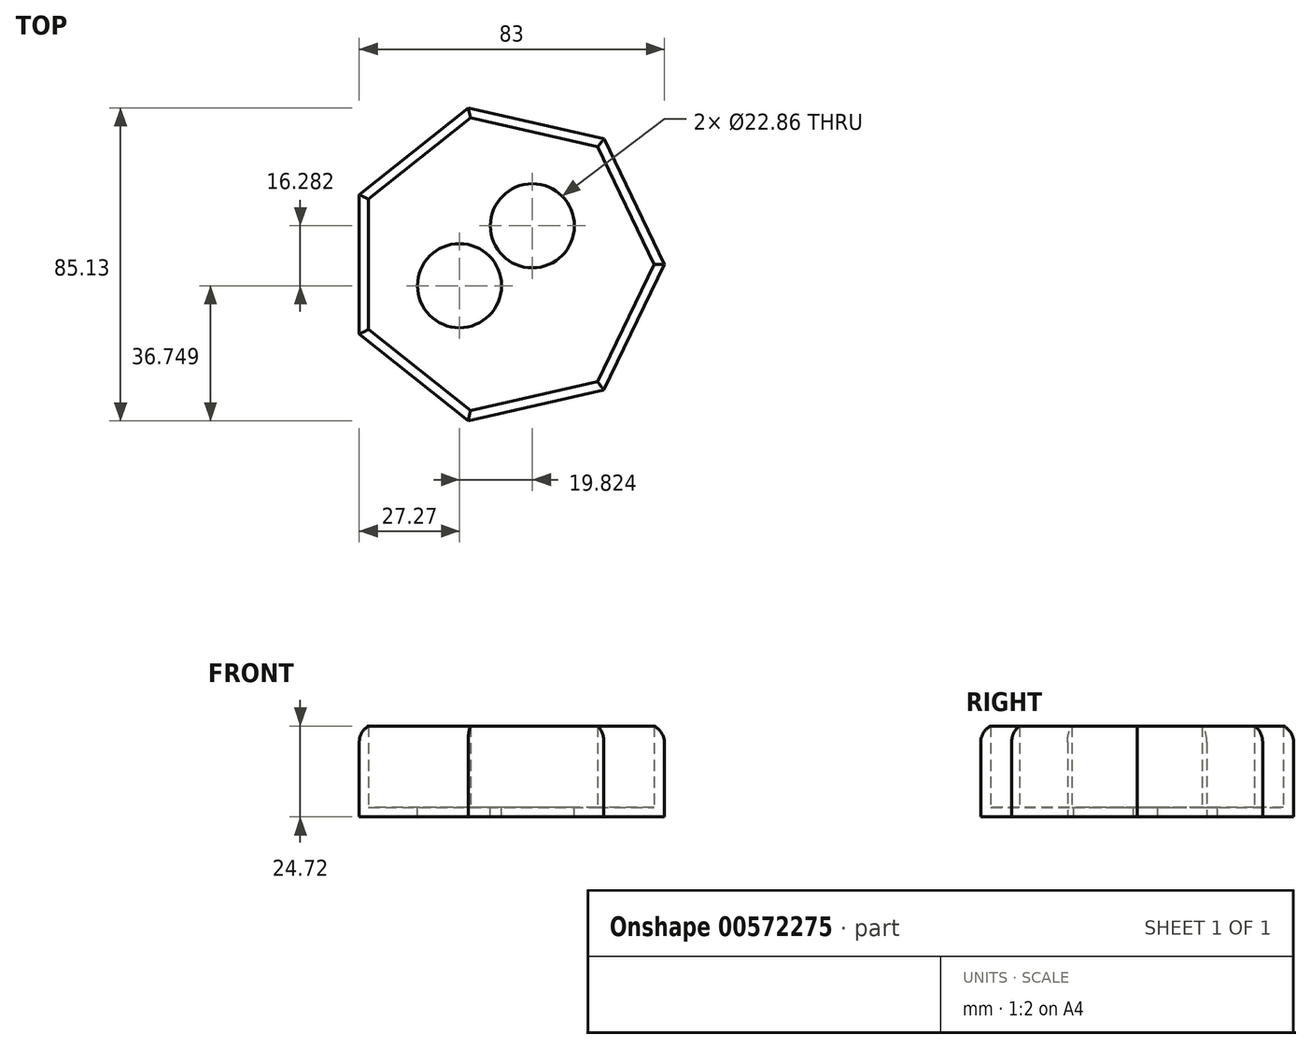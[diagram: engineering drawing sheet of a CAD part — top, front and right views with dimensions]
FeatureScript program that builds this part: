
annotation { "Feature Type Name" : "Feature", "Feature Type Description" : "" }
export const myFeature = defineFeature(function(context is Context, id is Id, definition is map)
    precondition{}
    {
        {
            var Q0;
            Q0=qCreatedBy(makeId("Top.planeOp"),FACE);
            var sketch = newSketch(context, id + "F0", { "sketchPlane" : qUnion([Q0])});
            skCircle(sketch, "E0.cCircle", {"center": v(0, 0) * mm, "radius": 39.34 * mm, "construction": true});
            skLineSegment(sketch, "E0.0", {"start": v(-9.7, 42.57) * mm, "end": v(27.23, 34.13) * mm});
            skLineSegment(sketch, "E0.1", {"start": v(27.23, 34.13) * mm, "end": v(43.66, 0) * mm});
            skLineSegment(sketch, "E0.2", {"start": v(43.66, 0) * mm, "end": v(27.22, -34.14) * mm});
            skLineSegment(sketch, "E0.3", {"start": v(27.22, -34.14) * mm, "end": v(-9.72, -42.56) * mm});
            skLineSegment(sketch, "E0.4", {"start": v(-9.72, -42.56) * mm, "end": v(-39.34, -18.94) * mm});
            skLineSegment(sketch, "E0.5", {"start": v(-39.34, -18.94) * mm, "end": v(-39.33, 18.95) * mm});
            skLineSegment(sketch, "E0.6", {"start": v(-39.33, 18.95) * mm, "end": v(-9.7, 42.57) * mm});
            skPoint(sketch, "E0.0.midPoint", {"position": v(8.76, 38.35) * mm});
            skSolve(sketch);
        }
        {
            var Q0;
            Q0=makeQuery(id+"F0.imprint","IMPRINT",FACE,{"disambiguationData":[TD([[makeQuery(id+"F0.imprint","IMPRINT",EDGE,{"derivedFrom":sQuery(id+"F0.wireOp",EDGE,"E0.0")}),-1.0]])]});
            extrude(context, id + "F1", {"entities" : qUnion([Q0]), "depth" : 25.4 * mm, "offsetDistance" : 25.4 * mm});
        }
        {
            var Q0;
            Q0=makeQuery(id+"F1.opExtrude","CAP_FACE",FACE,{"disambiguationData":[OSD([sQuery(id+"F0.wireOp",EDGE,"E0.0"),sQuery(id+"F0.wireOp",EDGE,"E0.1"),sQuery(id+"F0.wireOp",EDGE,"E0.2"),sQuery(id+"F0.wireOp",EDGE,"E0.3"),sQuery(id+"F0.wireOp",EDGE,"E0.4"),sQuery(id+"F0.wireOp",EDGE,"E0.5"),sQuery(id+"F0.wireOp",EDGE,"E0.6")])],"isStart":false});
            shell(context, id + "F2", {"entities" : qUnion([Q0]), "thickness" : 2.54 * mm});
        }
        {
            var Q0;
            Q0=makeQuery(id+"F2.opShell","OFFSET_FACE",FACE,{"disambiguationData":[OSD([sQuery(id+"F0.wireOp",EDGE,"E0.0"),sQuery(id+"F0.wireOp",EDGE,"E0.1"),sQuery(id+"F0.wireOp",EDGE,"E0.2"),sQuery(id+"F0.wireOp",EDGE,"E0.3"),sQuery(id+"F0.wireOp",EDGE,"E0.4"),sQuery(id+"F0.wireOp",EDGE,"E0.5"),sQuery(id+"F0.wireOp",EDGE,"E0.6")])]});
            var sketch = newSketch(context, id + "F3", { "sketchPlane" : qUnion([Q0])});
            skPoint(sketch, "E1", {"position": v(-12.07, -5.81) * mm});
            skSolve(sketch);
        }
        {
            var Q0;
            Q0=sQuery(id+"F3.wireOp",VERTEX,"E1");
            var Q1;
            Q1=makeQuery(id+"F1.opExtrude","SWEPT_BODY",BODY,{"disambiguationData":[OSD([sQuery(id+"F0.wireOp",EDGE,"E0.0"),sQuery(id+"F0.wireOp",EDGE,"E0.1"),sQuery(id+"F0.wireOp",EDGE,"E0.2"),sQuery(id+"F0.wireOp",EDGE,"E0.3"),sQuery(id+"F0.wireOp",EDGE,"E0.4"),sQuery(id+"F0.wireOp",EDGE,"E0.5"),sQuery(id+"F0.wireOp",EDGE,"E0.6")])]});
            hole(context, id + "F4", {"style" : HoleStyle.SIMPLE, "endStyle" : HoleEndStyle.THROUGH, "holeDiameter" : 22.86 * mm, "isTappedThrough" : true, "tappedDepth" : 12.7 * mm, "tapClearance" : 3, "locations" : qUnion([Q0]), "scope" : qUnion([Q1])});
        }
        {
            var Q0;
            Q0=makeQuery(id+"F2.opShell","OFFSET_FACE",FACE,{"disambiguationData":[OSD([sQuery(id+"F0.wireOp",EDGE,"E0.0"),sQuery(id+"F0.wireOp",EDGE,"E0.1"),sQuery(id+"F0.wireOp",EDGE,"E0.2"),sQuery(id+"F0.wireOp",EDGE,"E0.3"),sQuery(id+"F0.wireOp",EDGE,"E0.4"),sQuery(id+"F0.wireOp",EDGE,"E0.5"),sQuery(id+"F0.wireOp",EDGE,"E0.6")])]});
            var sketch = newSketch(context, id + "F5", { "sketchPlane" : qUnion([Q0])});
            skPoint(sketch, "E2", {"position": v(7.75, 10.47) * mm});
            skSolve(sketch);
        }
        {
            var Q0;
            Q0=sQuery(id+"F5.wireOp",VERTEX,"E2");
            var Q1;
            Q1=makeQuery(id+"F1.opExtrude","SWEPT_BODY",BODY,{"disambiguationData":[OSD([sQuery(id+"F0.wireOp",EDGE,"E0.0"),sQuery(id+"F0.wireOp",EDGE,"E0.1"),sQuery(id+"F0.wireOp",EDGE,"E0.2"),sQuery(id+"F0.wireOp",EDGE,"E0.3"),sQuery(id+"F0.wireOp",EDGE,"E0.4"),sQuery(id+"F0.wireOp",EDGE,"E0.5"),sQuery(id+"F0.wireOp",EDGE,"E0.6")])]});
            hole(context, id + "F6", {"style" : HoleStyle.SIMPLE, "endStyle" : HoleEndStyle.THROUGH, "holeDiameter" : 22.86 * mm, "isTappedThrough" : true, "tappedDepth" : 12.7 * mm, "tapClearance" : 3, "locations" : qUnion([Q0]), "scope" : qUnion([Q1])});
        }
        {
            var Q0;
            Q0=makeQuery(id+"F2.opShell","OFFSET_FACE",FACE,{"disambiguationData":[OSD([sQuery(id+"F0.wireOp",EDGE,"E0.0"),sQuery(id+"F0.wireOp",EDGE,"E0.1"),sQuery(id+"F0.wireOp",EDGE,"E0.2"),sQuery(id+"F0.wireOp",EDGE,"E0.3"),sQuery(id+"F0.wireOp",EDGE,"E0.4"),sQuery(id+"F0.wireOp",EDGE,"E0.5"),sQuery(id+"F0.wireOp",EDGE,"E0.6")])]});
            var sketch = newSketch(context, id + "F7", { "sketchPlane" : qUnion([Q0])});
            skArc(sketch, "E3", {"start": v(0, -15.74) * mm, "mid": v(12.86, -14.87) * mm, "end": v(16.41, -2.48) * mm});
            skSolve(sketch);
        }
        {
            var Q0;
            Q0=sQuery(id+"F7.wireOp",EDGE,"E3");
            extrude(context, id + "F8", {"bodyType" : ToolBodyType.SURFACE, "surfaceEntities" : qUnion([Q0]), "depth" : 12.7 * mm, "offsetDistance" : 25.4 * mm});
        }
        {
            var Q0;
            Q0=makeQuery(id+"F1.opExtrude","CAP_EDGE",EDGE,{"disambiguationData":[OSD([sQuery(id+"F0.wireOp",EDGE,"E0.0")])],"isStart":false});
            var Q1;
            Q1=makeQuery(id+"F1.opExtrude","CAP_EDGE",EDGE,{"disambiguationData":[OSD([sQuery(id+"F0.wireOp",EDGE,"E0.6")])],"isStart":false});
            var Q2;
            Q2=makeQuery(id+"F1.opExtrude","CAP_EDGE",EDGE,{"disambiguationData":[OSD([sQuery(id+"F0.wireOp",EDGE,"E0.5")])],"isStart":false});
            var Q3;
            Q3=makeQuery(id+"F1.opExtrude","CAP_EDGE",EDGE,{"disambiguationData":[OSD([sQuery(id+"F0.wireOp",EDGE,"E0.4")])],"isStart":false});
            var Q4;
            Q4=makeQuery(id+"F1.opExtrude","CAP_EDGE",EDGE,{"disambiguationData":[OSD([sQuery(id+"F0.wireOp",EDGE,"E0.3")])],"isStart":false});
            var Q5;
            Q5=makeQuery(id+"F1.opExtrude","CAP_EDGE",EDGE,{"disambiguationData":[OSD([sQuery(id+"F0.wireOp",EDGE,"E0.2")])],"isStart":false});
            var Q6;
            Q6=makeQuery(id+"F1.opExtrude","CAP_EDGE",EDGE,{"disambiguationData":[OSD([sQuery(id+"F0.wireOp",EDGE,"E0.1")])],"isStart":false});
            fillet(context, id + "F9", {"entities" : qUnion([Q0, Q1, Q2, Q3, Q4, Q5, Q6]), "radius" : 5.08 * mm, "tangentPropagation" : true, "allowEdgeOverflow" : false});
        }
    });
